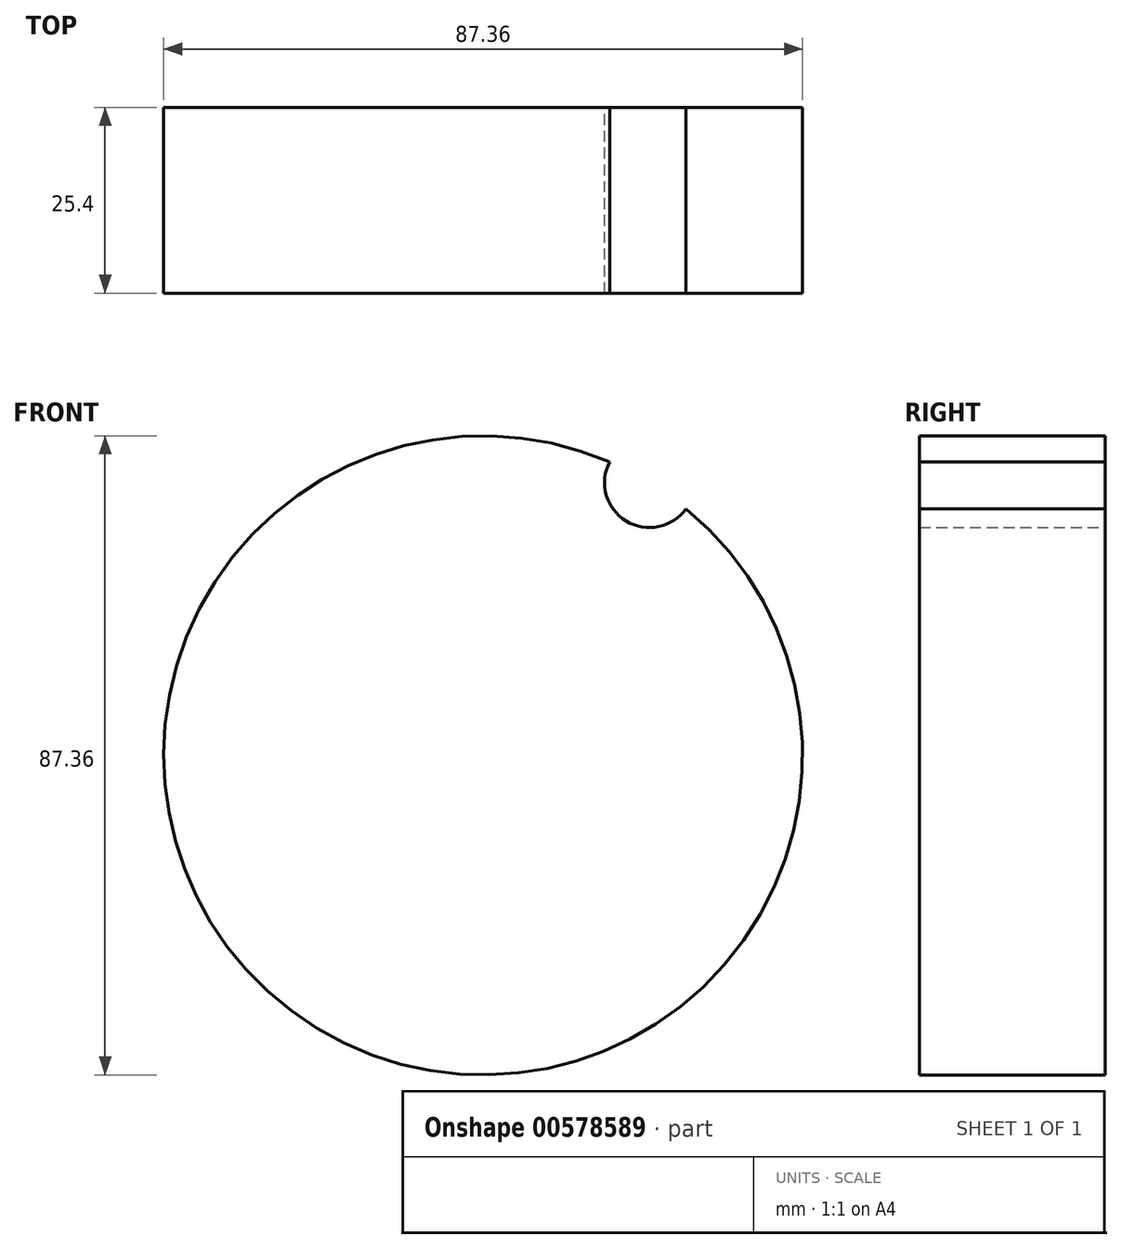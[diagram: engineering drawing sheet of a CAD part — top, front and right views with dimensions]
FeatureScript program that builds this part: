
annotation { "Feature Type Name" : "Feature", "Feature Type Description" : "" }
export const myFeature = defineFeature(function(context is Context, id is Id, definition is map)
    precondition{}
    {
        {
            var Q0;
            Q0=qCreatedBy(makeId("Front.planeOp"),FACE);
            var sketch = newSketch(context, id + "F0", { "sketchPlane" : qUnion([Q0])});
            skArc(sketch, "E0", {"start": v(17.29, 40.1) * mm, "mid": v(-22.75, -37.29) * mm, "end": v(27.76, 33.72) * mm});
            skArc(sketch, "E1", {"start": v(17.29, 40.1) * mm, "mid": v(19.55, 32.04) * mm, "end": v(27.76, 33.72) * mm});
            skSolve(sketch);
        }
        {
            var Q0;
            Q0=makeQuery(id+"F0.imprint","IMPRINT",FACE,{"disambiguationData":[TD([[makeQuery(id+"F0.imprint","IMPRINT",EDGE,{"derivedFrom":sQuery(id+"F0.wireOp",EDGE,"E0")}),1.0]])]});
            extrude(context, id + "F1", {"entities" : qUnion([Q0]), "depth" : 25.4 * mm, "offsetDistance" : 25.4 * mm});
        }
    });
